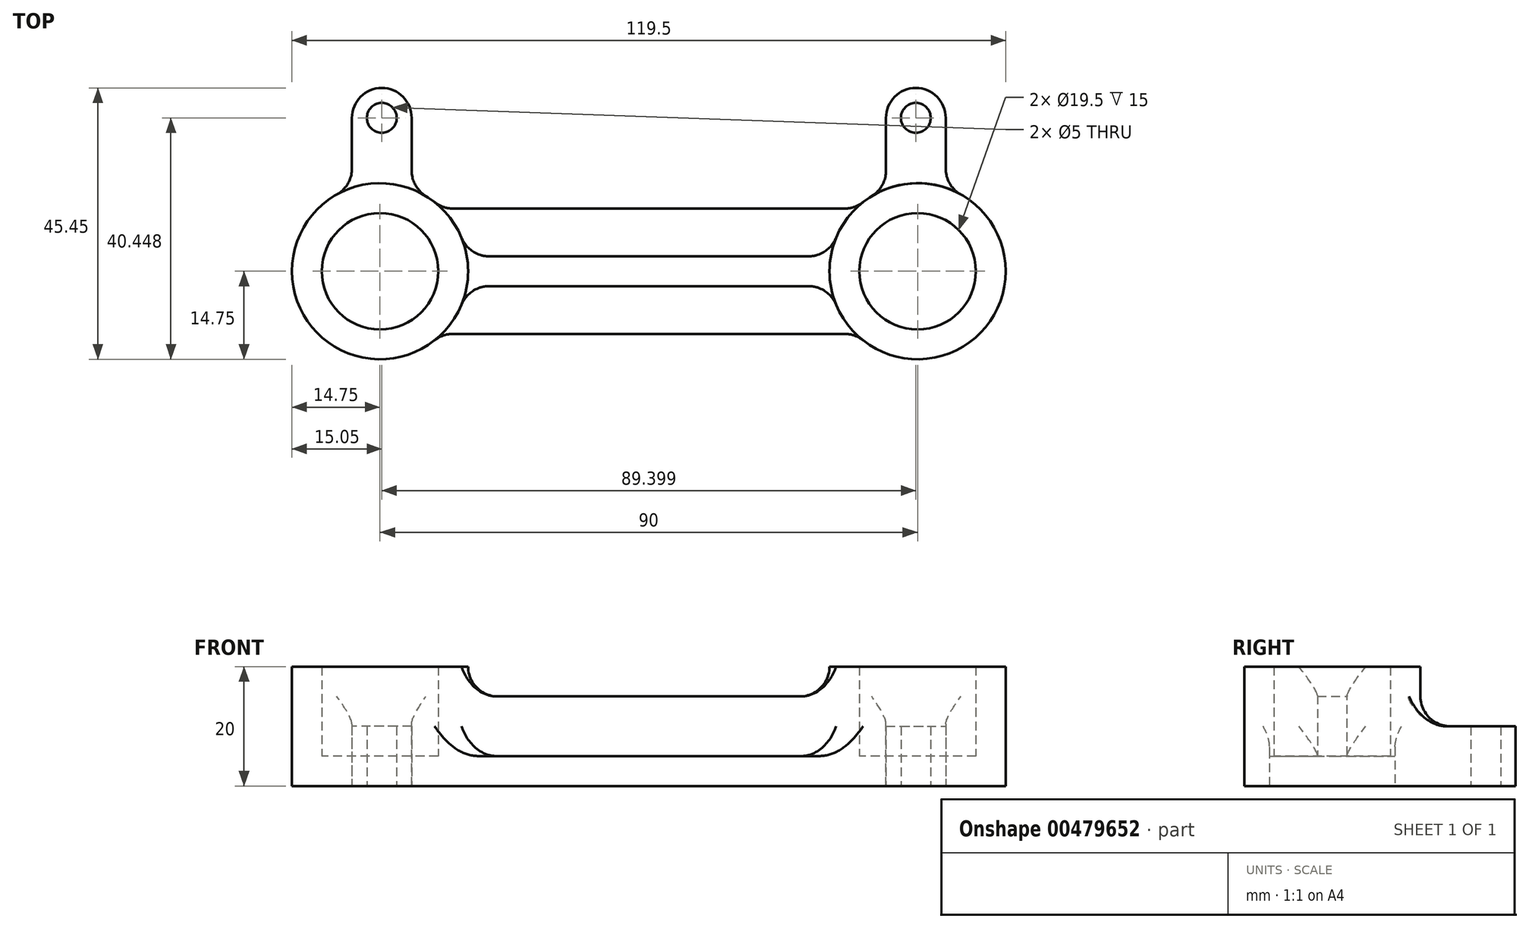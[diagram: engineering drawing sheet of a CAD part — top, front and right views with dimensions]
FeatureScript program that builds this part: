
annotation { "Feature Type Name" : "Feature", "Feature Type Description" : "" }
export const myFeature = defineFeature(function(context is Context, id is Id, definition is map)
    precondition{}
    {
        {
            var Q0;
            Q0=qCreatedBy(makeId("Top.planeOp"),FACE);
            var sketch = newSketch(context, id + "F0", { "sketchPlane" : qUnion([Q0])});
            skLineSegment(sketch, "E0.bottom", {"start": v(45, 9.75) * mm, "end": v(-45, 9.75) * mm});
            skLineSegment(sketch, "E0.top", {"start": v(45, -9.75) * mm, "end": v(-45, -9.75) * mm});
            skPoint(sketch, "E0.middle", {"position": v(0, 0) * mm});
            skCircle(sketch, "E1", {"center": v(-45, 0) * mm, "radius": 9.75 * mm});
            skCircle(sketch, "E2.0", {"center": v(-45, 0) * mm, "radius": 14.75 * mm});
            skCircle(sketch, "E3.MirrorC", {"center": v(45, 0) * mm, "radius": 14.75 * mm});
            skCircle(sketch, "E4.MirrorC", {"center": v(45, 0) * mm, "radius": 9.75 * mm});
            skSolve(sketch);
        }
        {
            var Q0;
            {var subQ0=sQuery(id+"F0.wireOp",EDGE,"E1");var subQ1=sQuery(id+"F0.wireOp",EDGE,"E0.bottom");var subQ2=makeQuery(id+"F0.imprint","INTERSECT",VERTEX,{"derivedFrom":[subQ1,subQ0]});Q0=makeQuery(id+"F0.imprint","IMPRINT",FACE,{"disambiguationData":[TD([[makeQuery(id+"F0.imprint","IMPRINT",EDGE,{"disambiguationData":[TD([[subQ2,1.0]])],"derivedFrom":subQ1}),-1.0]])]});}
            var Q1;
            {var subQ0=sQuery(id+"F0.wireOp",EDGE,"E1");var subQ1=sQuery(id+"F0.wireOp",EDGE,"E0.bottom");var subQ2=makeQuery(id+"F0.imprint","INTERSECT",VERTEX,{"derivedFrom":[subQ1,subQ0]});Q1=makeQuery(id+"F0.imprint","IMPRINT",FACE,{"disambiguationData":[TD([[makeQuery(id+"F0.imprint","IMPRINT",EDGE,{"disambiguationData":[TD([[subQ2,1.0]])],"derivedFrom":subQ1}),1.0]])]});}
            var Q2;
            {var subQ0=sQuery(id+"F0.wireOp",EDGE,"E4.MirrorC");var subQ1=sQuery(id+"F0.wireOp",EDGE,"E0.bottom");var subQ2=makeQuery(id+"F0.imprint","INTERSECT",VERTEX,{"derivedFrom":[subQ1,subQ0]});Q2=makeQuery(id+"F0.imprint","IMPRINT",FACE,{"disambiguationData":[TD([[makeQuery(id+"F0.imprint","IMPRINT",EDGE,{"disambiguationData":[TD([[subQ2,-1.0]])],"derivedFrom":subQ1}),1.0]])]});}
            var Q3;
            {var subQ0=sQuery(id+"F0.wireOp",EDGE,"E4.MirrorC");var subQ1=sQuery(id+"F0.wireOp",EDGE,"E0.bottom");var subQ2=makeQuery(id+"F0.imprint","INTERSECT",VERTEX,{"derivedFrom":[subQ1,subQ0]});Q3=makeQuery(id+"F0.imprint","IMPRINT",FACE,{"disambiguationData":[TD([[makeQuery(id+"F0.imprint","IMPRINT",EDGE,{"disambiguationData":[TD([[subQ2,-1.0]])],"derivedFrom":subQ1}),-1.0]])]});}
            extrude(context, id + "F1", {"entities" : qUnion([Q0, Q1, Q2, Q3]), "depth" : 20 * mm, "offsetDistance" : 25 * mm});
        }
        {
            var Q0;
            Q0=qCreatedBy(makeId("Top.planeOp"),FACE);
            var sketch = newSketch(context, id + "F2", { "sketchPlane" : qUnion([Q0])});
            skLineSegment(sketch, "E5.bottom", {"start": v(-55, 10.5) * mm, "end": v(55, 10.5) * mm});
            skLineSegment(sketch, "E5.top", {"start": v(-55, -10.5) * mm, "end": v(55, -10.5) * mm});
            skLineSegment(sketch, "E5.left", {"start": v(-55, 10.5) * mm, "end": v(-55, -10.5) * mm});
            skLineSegment(sketch, "E5.right", {"start": v(55, 10.5) * mm, "end": v(55, -10.5) * mm});
            skPoint(sketch, "E5.middle", {"position": v(0, 0) * mm});
            skSolve(sketch);
        }
        {
            var Q0;
            Q0=makeQuery(id+"F2.imprint","IMPRINT",FACE,{"disambiguationData":[TD([[makeQuery(id+"F2.imprint","IMPRINT",EDGE,{"derivedFrom":sQuery(id+"F2.wireOp",EDGE,"E5.bottom")}),-1.0]])]});
            extrude(context, id + "F3", {"entities" : qUnion([Q0]), "depth" : 5 * mm, "offsetDistance" : 25 * mm});
        }
        {
            var Q0;
            Q0=qCreatedBy(makeId("Top.planeOp"),FACE);
            var sketch = newSketch(context, id + "F4", { "sketchPlane" : qUnion([Q0])});
            skLineSegment(sketch, "E6.bottom", {"start": v(34, -2.5) * mm, "end": v(-34, -2.5) * mm});
            skLineSegment(sketch, "E6.top", {"start": v(34, 2.5) * mm, "end": v(-34, 2.5) * mm});
            skLineSegment(sketch, "E6.left", {"start": v(34, -2.5) * mm, "end": v(34, 2.5) * mm});
            skLineSegment(sketch, "E6.right", {"start": v(-34, -2.5) * mm, "end": v(-34, 2.5) * mm});
            skPoint(sketch, "E6.middle", {"position": v(0, 0) * mm});
            skSolve(sketch);
        }
        {
            var Q0;
            Q0=makeQuery(id+"F4.imprint","IMPRINT",FACE,{"disambiguationData":[TD([[makeQuery(id+"F4.imprint","IMPRINT",EDGE,{"derivedFrom":sQuery(id+"F4.wireOp",EDGE,"E6.bottom")}),-1.0]])]});
            extrude(context, id + "F5", {"entities" : qUnion([Q0]), "depth" : 15 * mm, "offsetDistance" : 25 * mm});
        }
        {
            var Q0;
            Q0=makeQuery(id+"F5.opExtrude","SWEPT_BODY",BODY,{"disambiguationData":[OSD([sQuery(id+"F4.wireOp",EDGE,"E6.bottom"),sQuery(id+"F4.wireOp",EDGE,"E6.top"),sQuery(id+"F4.wireOp",EDGE,"E6.left"),sQuery(id+"F4.wireOp",EDGE,"E6.right")])]});
            var Q1;
            Q1=makeQuery(id+"F1.opExtrude","SWEPT_BODY",BODY,{"disambiguationData":[OSD([sQuery(id+"F0.wireOp",EDGE,"E3.MirrorC"),sQuery(id+"F0.wireOp",EDGE,"E4.MirrorC")])]});
            var Q2;
            Q2=makeQuery(id+"F3.opExtrude","SWEPT_BODY",BODY,{"disambiguationData":[OSD([sQuery(id+"F2.wireOp",EDGE,"E5.bottom"),sQuery(id+"F2.wireOp",EDGE,"E5.top"),sQuery(id+"F2.wireOp",EDGE,"E5.left"),sQuery(id+"F2.wireOp",EDGE,"E5.right")])]});
            var Q3;
            Q3=makeQuery(id+"F1.opExtrude","SWEPT_BODY",BODY,{"disambiguationData":[OSD([sQuery(id+"F0.wireOp",EDGE,"E1"),sQuery(id+"F0.wireOp",EDGE,"E2.0")])]});
            booleanBodies(context, id + "F6", {"operationType" : BooleanOperationType.UNION, "tools" : qUnion([Q0, Q1, Q2, Q3])});
        }
        {
            var Q0;
            Q0=makeQuery(id+"F6.opBoolean","INTERSECT",EDGE,{"disambiguationData":[OD(1.0)],"derivedFrom":[makeQuery(id+"F1.opExtrude","SWEPT_FACE",FACE,{"disambiguationData":[OSD([sQuery(id+"F0.wireOp",EDGE,"E3.MirrorC")])]}),makeQuery(id+"F3.opExtrude","CAP_FACE",FACE,{"disambiguationData":[OSD([sQuery(id+"F2.wireOp",EDGE,"E5.bottom"),sQuery(id+"F2.wireOp",EDGE,"E5.top"),sQuery(id+"F2.wireOp",EDGE,"E5.left"),sQuery(id+"F2.wireOp",EDGE,"E5.right")])],"isStart":false})]});
            var Q1;
            Q1=makeQuery(id+"F6.opBoolean","INTERSECT",EDGE,{"derivedFrom":[makeQuery(id+"F1.opExtrude","SWEPT_FACE",FACE,{"disambiguationData":[OSD([sQuery(id+"F0.wireOp",EDGE,"E3.MirrorC")])]}),makeQuery(id+"F5.opExtrude","SWEPT_FACE",FACE,{"disambiguationData":[OSD([sQuery(id+"F4.wireOp",EDGE,"E6.bottom")])]})]});
            var Q2;
            Q2=makeQuery(id+"F6.opBoolean","INTERSECT",EDGE,{"derivedFrom":[makeQuery(id+"F1.opExtrude","SWEPT_FACE",FACE,{"disambiguationData":[OSD([sQuery(id+"F0.wireOp",EDGE,"E3.MirrorC")])]}),makeQuery(id+"F5.opExtrude","CAP_FACE",FACE,{"disambiguationData":[OSD([sQuery(id+"F4.wireOp",EDGE,"E6.bottom"),sQuery(id+"F4.wireOp",EDGE,"E6.top"),sQuery(id+"F4.wireOp",EDGE,"E6.left"),sQuery(id+"F4.wireOp",EDGE,"E6.right")])],"isStart":false})]});
            var Q3;
            Q3=makeQuery(id+"F6.opBoolean","INTERSECT",EDGE,{"disambiguationData":[OD(0.0)],"derivedFrom":[makeQuery(id+"F1.opExtrude","SWEPT_FACE",FACE,{"disambiguationData":[OSD([sQuery(id+"F0.wireOp",EDGE,"E3.MirrorC")])]}),makeQuery(id+"F3.opExtrude","CAP_FACE",FACE,{"disambiguationData":[OSD([sQuery(id+"F2.wireOp",EDGE,"E5.bottom"),sQuery(id+"F2.wireOp",EDGE,"E5.top"),sQuery(id+"F2.wireOp",EDGE,"E5.left"),sQuery(id+"F2.wireOp",EDGE,"E5.right")])],"isStart":false})]});
            var Q4;
            Q4=makeQuery(id+"F6.opBoolean","INTERSECT",EDGE,{"derivedFrom":[makeQuery(id+"F1.opExtrude","SWEPT_FACE",FACE,{"disambiguationData":[OSD([sQuery(id+"F0.wireOp",EDGE,"E2.0")])]}),makeQuery(id+"F5.opExtrude","SWEPT_FACE",FACE,{"disambiguationData":[OSD([sQuery(id+"F4.wireOp",EDGE,"E6.top")])]})]});
            var Q5;
            Q5=makeQuery(id+"F6.opBoolean","INTERSECT",EDGE,{"disambiguationData":[OD(0.0)],"derivedFrom":[makeQuery(id+"F1.opExtrude","SWEPT_FACE",FACE,{"disambiguationData":[OSD([sQuery(id+"F0.wireOp",EDGE,"E2.0")])]}),makeQuery(id+"F3.opExtrude","CAP_FACE",FACE,{"disambiguationData":[OSD([sQuery(id+"F2.wireOp",EDGE,"E5.bottom"),sQuery(id+"F2.wireOp",EDGE,"E5.top"),sQuery(id+"F2.wireOp",EDGE,"E5.left"),sQuery(id+"F2.wireOp",EDGE,"E5.right")])],"isStart":false})]});
            var Q6;
            Q6=makeQuery(id+"F6.opBoolean","INTERSECT",EDGE,{"disambiguationData":[OD(1.0)],"derivedFrom":[makeQuery(id+"F1.opExtrude","SWEPT_FACE",FACE,{"disambiguationData":[OSD([sQuery(id+"F0.wireOp",EDGE,"E2.0")])]}),makeQuery(id+"F3.opExtrude","CAP_FACE",FACE,{"disambiguationData":[OSD([sQuery(id+"F2.wireOp",EDGE,"E5.bottom"),sQuery(id+"F2.wireOp",EDGE,"E5.top"),sQuery(id+"F2.wireOp",EDGE,"E5.left"),sQuery(id+"F2.wireOp",EDGE,"E5.right")])],"isStart":false})]});
            var Q7;
            Q7=makeQuery(id+"F6.opBoolean","INTERSECT",EDGE,{"derivedFrom":[makeQuery(id+"F1.opExtrude","SWEPT_FACE",FACE,{"disambiguationData":[OSD([sQuery(id+"F0.wireOp",EDGE,"E2.0")])]}),makeQuery(id+"F5.opExtrude","CAP_FACE",FACE,{"disambiguationData":[OSD([sQuery(id+"F4.wireOp",EDGE,"E6.bottom"),sQuery(id+"F4.wireOp",EDGE,"E6.top"),sQuery(id+"F4.wireOp",EDGE,"E6.left"),sQuery(id+"F4.wireOp",EDGE,"E6.right")])],"isStart":false})]});
            fillet(context, id + "F7", {"entities" : qUnion([Q0, Q1, Q2, Q3, Q4, Q5, Q6, Q7]), "radius" : 5 * mm, "tangentPropagation" : true, "allowEdgeOverflow" : false});
        }
        {
            var Q0;
            Q0=qCreatedBy(makeId("Top.planeOp"),FACE);
            var sketch = newSketch(context, id + "F8", { "sketchPlane" : qUnion([Q0])});
            skLineSegment(sketch, "E7.bottom", {"start": v(-49.7, 13.47) * mm, "end": v(-39.7, 13.47) * mm});
            skLineSegment(sketch, "E7.top", {"start": v(-44.7, 30.7) * mm, "end": v(-44.7, 30.7) * mm});
            skLineSegment(sketch, "E7.left", {"start": v(-49.7, 13.47) * mm, "end": v(-49.7, 25.7) * mm});
            skLineSegment(sketch, "E7.right", {"start": v(-39.7, 13.47) * mm, "end": v(-39.7, 25.7) * mm});
            skPoint(sketch, "E8.visualSharp", {"position": v(-39.7, 30.7) * mm});
            skArc(sketch, "E8.filletArc", {"start": v(-39.7, 25.7) * mm, "mid": v(-41.16, 29.23) * mm, "end": v(-44.7, 30.7) * mm});
            skPoint(sketch, "E9.visualSharp", {"position": v(-49.7, 30.7) * mm});
            skArc(sketch, "E9.filletArc", {"start": v(-44.7, 30.7) * mm, "mid": v(-48.23, 29.23) * mm, "end": v(-49.7, 25.7) * mm});
            skCircle(sketch, "E10", {"center": v(-44.7, 25.7) * mm, "radius": 2.5 * mm});
            skPoint(sketch, "E11.orphan", {"position": v(-43.98, 0) * mm});
            skPoint(sketch, "E12.end.orphan", {"position": v(-43.98, 30.7) * mm});
            skSolve(sketch);
        }
        {
            var Q0;
            Q0=makeQuery(id+"F8.imprint","IMPRINT",FACE,{"disambiguationData":[TD([[makeQuery(id+"F8.imprint","IMPRINT",EDGE,{"derivedFrom":sQuery(id+"F8.wireOp",EDGE,"E7.bottom")}),1.0]])]});
            extrude(context, id + "F9", {"entities" : qUnion([Q0]), "operationType" : NewBodyOperationType.ADD, "depth" : 10 * mm, "offsetDistance" : 25 * mm});
        }
        {
            var Q0;
            Q0=makeQuery(id+"F9.boolean.opBoolean","INTERSECT",EDGE,{"derivedFrom":[makeQuery(id+"F1.opExtrude","SWEPT_FACE",FACE,{"disambiguationData":[OSD([sQuery(id+"F0.wireOp",EDGE,"E2.0")])]}),makeQuery(id+"F9.opExtrude","CAP_FACE",FACE,{"disambiguationData":[OSD([sQuery(id+"F8.wireOp",EDGE,"E7.bottom"),sQuery(id+"F8.wireOp",EDGE,"E7.left"),sQuery(id+"F8.wireOp",EDGE,"E7.right"),sQuery(id+"F8.wireOp",EDGE,"E8.filletArc"),sQuery(id+"F8.wireOp",EDGE,"E9.filletArc"),sQuery(id+"F8.wireOp",EDGE,"E10")])],"isStart":false})]});
            var Q1;
            Q1=makeQuery(id+"F9.boolean.opBoolean","INTERSECT",EDGE,{"derivedFrom":[makeQuery(id+"F1.opExtrude","SWEPT_FACE",FACE,{"disambiguationData":[OSD([sQuery(id+"F0.wireOp",EDGE,"E2.0")])]}),makeQuery(id+"F9.opExtrude","SWEPT_FACE",FACE,{"disambiguationData":[OSD([sQuery(id+"F8.wireOp",EDGE,"E7.left")])]})]});
            var Q2;
            Q2=makeQuery(id+"F9.boolean.opBoolean","INTERSECT",EDGE,{"derivedFrom":[makeQuery(id+"F1.opExtrude","SWEPT_FACE",FACE,{"disambiguationData":[OSD([sQuery(id+"F0.wireOp",EDGE,"E2.0")])]}),makeQuery(id+"F9.opExtrude","SWEPT_FACE",FACE,{"disambiguationData":[OSD([sQuery(id+"F8.wireOp",EDGE,"E7.right")])]})]});
            fillet(context, id + "F10", {"entities" : qUnion([Q0, Q1, Q2]), "radius" : 5 * mm, "tangentPropagation" : true, "allowEdgeOverflow" : false});
        }
        {
            var Q0;
            Q0=makeQuery(id+"F5.opExtrude","SWEPT_BODY",BODY,{"disambiguationData":[OSD([sQuery(id+"F4.wireOp",EDGE,"E6.bottom"),sQuery(id+"F4.wireOp",EDGE,"E6.top"),sQuery(id+"F4.wireOp",EDGE,"E6.left"),sQuery(id+"F4.wireOp",EDGE,"E6.right")])]});
            var Q1;
            Q1=qCreatedBy(makeId("Right.planeOp"),FACE);
            mirror(context, id + "F11", {"operationType" : NewBodyOperationType.ADD, "entities" : qUnion([Q0]), "mirrorPlane" : qUnion([Q1])});
        }
        {
            var Q0;
            Q0=makeQuery(id+"F6.opBoolean","INTERSECT",EDGE,{"derivedFrom":[makeQuery(id+"F1.opExtrude","SWEPT_FACE",FACE,{"disambiguationData":[OSD([sQuery(id+"F0.wireOp",EDGE,"E3.MirrorC")])]}),makeQuery(id+"F3.opExtrude","SWEPT_FACE",FACE,{"disambiguationData":[OSD([sQuery(id+"F2.wireOp",EDGE,"E5.bottom")])]})]});
            var Q1;
            Q1=makeQuery(id+"F6.opBoolean","INTERSECT",EDGE,{"derivedFrom":[makeQuery(id+"F1.opExtrude","SWEPT_FACE",FACE,{"disambiguationData":[OSD([sQuery(id+"F0.wireOp",EDGE,"E2.0")])]}),makeQuery(id+"F3.opExtrude","SWEPT_FACE",FACE,{"disambiguationData":[OSD([sQuery(id+"F2.wireOp",EDGE,"E5.bottom")])]})]});
            var Q2;
            Q2=makeQuery(id+"F6.opBoolean","INTERSECT",EDGE,{"derivedFrom":[makeQuery(id+"F1.opExtrude","SWEPT_FACE",FACE,{"disambiguationData":[OSD([sQuery(id+"F0.wireOp",EDGE,"E3.MirrorC")])]}),makeQuery(id+"F3.opExtrude","SWEPT_FACE",FACE,{"disambiguationData":[OSD([sQuery(id+"F2.wireOp",EDGE,"E5.top")])]})]});
            var Q3;
            Q3=makeQuery(id+"F6.opBoolean","INTERSECT",EDGE,{"derivedFrom":[makeQuery(id+"F1.opExtrude","SWEPT_FACE",FACE,{"disambiguationData":[OSD([sQuery(id+"F0.wireOp",EDGE,"E2.0")])]}),makeQuery(id+"F3.opExtrude","SWEPT_FACE",FACE,{"disambiguationData":[OSD([sQuery(id+"F2.wireOp",EDGE,"E5.top")])]})]});
            fillet(context, id + "F12", {"entities" : qUnion([Q0, Q1, Q2, Q3]), "radius" : 5 * mm, "tangentPropagation" : true, "allowEdgeOverflow" : false});
        }
    });
